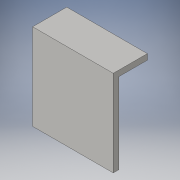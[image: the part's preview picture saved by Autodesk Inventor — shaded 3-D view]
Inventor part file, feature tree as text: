
AUTODESK INVENTOR PART (.ipt)
format: ipt  version: 2016 (Build 200138000, 138)  size: 100,352 bytes
history: native  units: in
note: dims shown in document units (in); Inventor stores cm internally (conversion verified against a paired STEP export)
features: extrude x3, sketch x3
ambient origin geometry x8: Origin, YZ Plane, XZ Plane, XY Plane, X Axis, Y Axis, Z Axis, Center Point
bodies: Solid1 (feature_tree)
feature tree (6):
  extrude  "Extrusion1"  Depth=0.709in
  extrude  "Extrusion2"  Depth=0.05in
  extrude  "Extrusion3"  Depth=0.05in TaperAngle=0.0deg
  sketch  "Sketch1"  dims[d0=0.709in d1=0.709in]
  sketch  "Sketch2"  dims[d2=0.05in d3=0.0in d4=0.25in]
  sketch  "Sketch3"  dims[d5=0.05in d6=0.0in d7=0.05in d8=0.0in]
